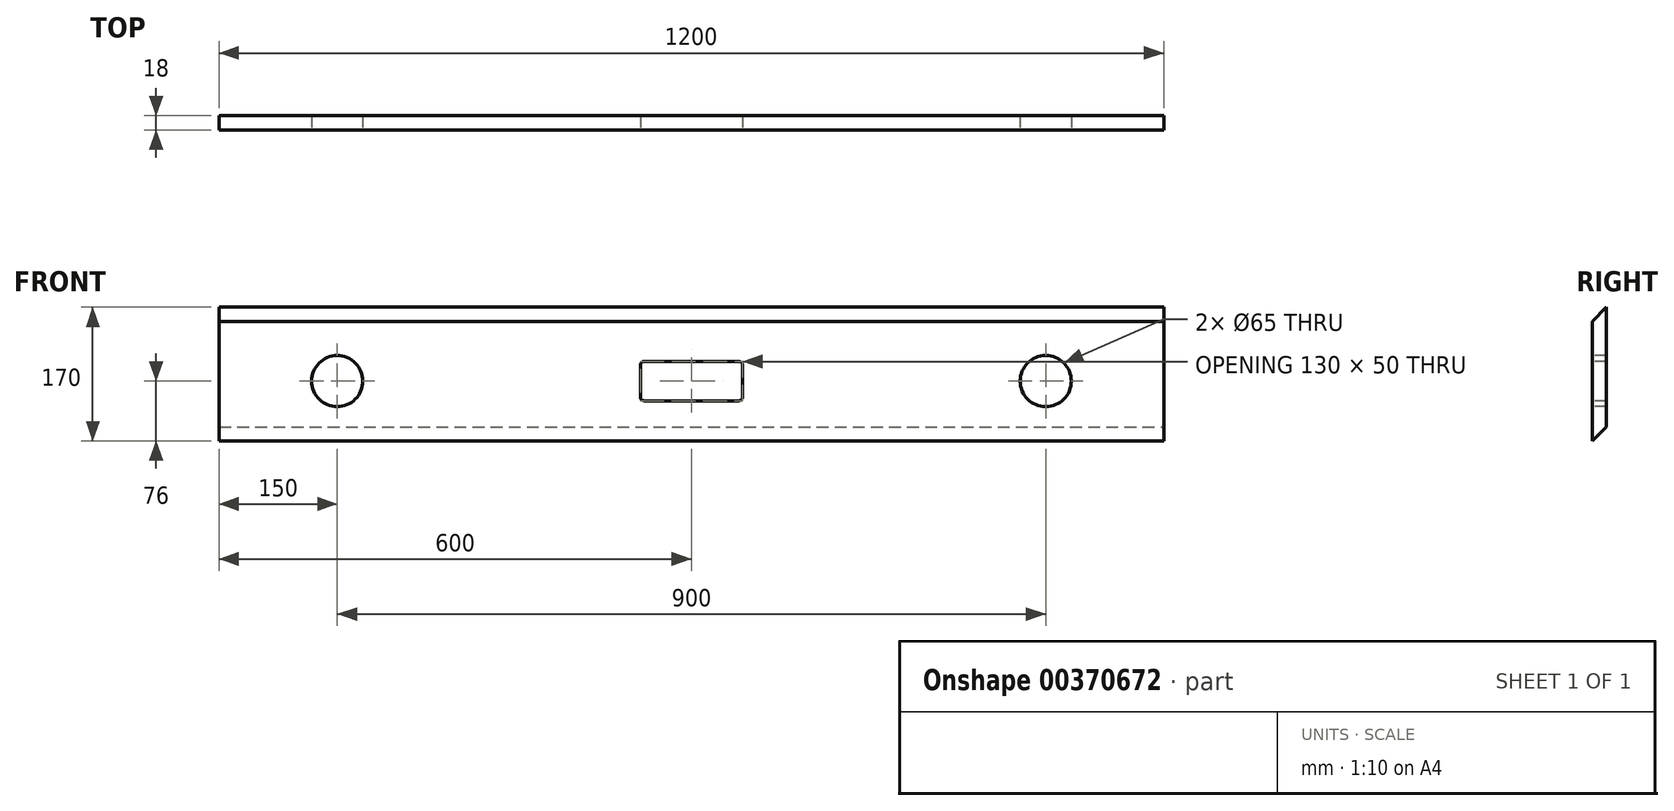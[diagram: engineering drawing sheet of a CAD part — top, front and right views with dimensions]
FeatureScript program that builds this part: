
annotation { "Feature Type Name" : "Feature", "Feature Type Description" : "" }
export const myFeature = defineFeature(function(context is Context, id is Id, definition is map)
    precondition{}
    {
        {
            var Q0;
            Q0=qCreatedBy(makeId("Front.planeOp"),FACE);
            var sketch = newSketch(context, id + "F0", { "sketchPlane" : qUnion([Q0])});
            skLineSegment(sketch, "E0.bottom", {"start": v(0, 0) * mm, "end": v(1200, 0) * mm});
            skLineSegment(sketch, "E0.top", {"start": v(0, 170) * mm, "end": v(1200, 170) * mm});
            skLineSegment(sketch, "E0.left", {"start": v(0, 0) * mm, "end": v(0, 170) * mm});
            skLineSegment(sketch, "E0.right", {"start": v(1200, 0) * mm, "end": v(1200, 170) * mm});
            skSolve(sketch);
        }
        {
            var Q0;
            Q0 = qSketchRegion(id + "F0", true);
            extrude(context, id + "F1", {"entities" : qUnion([Q0]), "depth" : 18 * mm});
        }
        {
            var Q0;
            Q0=makeQuery(id+"F1.opExtrude","SWEPT_FACE",FACE,{"disambiguationData":[OSD([sQuery(id+"F0.wireOp",EDGE,"E0.right")])]});
            var sketch = newSketch(context, id + "F2", { "sketchPlane" : qUnion([Q0])});
            skLineSegment(sketch, "E1", {"start": v(0, 170) * mm, "end": v(-18, 152) * mm});
            skLineSegment(sketch, "E2", {"start": v(-18, 152) * mm, "end": v(-18, 170) * mm});
            skLineSegment(sketch, "E3", {"start": v(-18, 170) * mm, "end": v(0, 170) * mm});
            skLineSegment(sketch, "E4", {"start": v(0, 0) * mm, "end": v(0, 18) * mm});
            skLineSegment(sketch, "E5", {"start": v(0, 18) * mm, "end": v(-18, 0) * mm});
            skLineSegment(sketch, "E6", {"start": v(-18, 0) * mm, "end": v(0, 0) * mm});
            skSolve(sketch);
        }
        {
            var Q0;
            Q0 = qSketchRegion(id + "F2", true);
            extrude(context, id + "F3", {"entities" : qUnion([Q0]), "operationType" : NewBodyOperationType.REMOVE, "endBound" : BoundingType.THROUGH_ALL, "oppositeDirection" : true, "depth" : 25 * mm});
        }
        {
            var Q0;
            Q0=makeQuery(id+"F1.opExtrude","CAP_FACE",FACE,{"disambiguationData":[OSD([sQuery(id+"F0.wireOp",EDGE,"E0.bottom"),sQuery(id+"F0.wireOp",EDGE,"E0.top"),sQuery(id+"F0.wireOp",EDGE,"E0.left"),sQuery(id+"F0.wireOp",EDGE,"E0.right")])],"isStart":false});
            var sketch = newSketch(context, id + "F4", { "sketchPlane" : qUnion([Q0])});
            skLineSegment(sketch, "E7", {"start": v(0, 76) * mm, "end": v(1200, 76) * mm, "construction": true});
            skLineSegment(sketch, "E8", {"start": v(600, 152) * mm, "end": v(600, 0) * mm, "construction": true});
            skCircle(sketch, "E9", {"center": v(150, 76) * mm, "radius": 32.5 * mm});
            skCircle(sketch, "E10", {"center": v(1050, 76) * mm, "radius": 32.5 * mm});
            skLineSegment(sketch, "E11.bottom", {"start": v(660, 51) * mm, "end": v(540, 51) * mm});
            skLineSegment(sketch, "E11.top", {"start": v(660, 101) * mm, "end": v(540, 101) * mm});
            skLineSegment(sketch, "E11.left", {"start": v(665, 56) * mm, "end": v(665, 96) * mm});
            skLineSegment(sketch, "E11.right", {"start": v(535, 56) * mm, "end": v(535, 96) * mm});
            skPoint(sketch, "E11.middle", {"position": v(600, 76) * mm});
            skPoint(sketch, "E12.visualSharp", {"position": v(535, 101) * mm});
            skArc(sketch, "E12.filletArc", {"start": v(540, 101) * mm, "mid": v(536.46, 99.54) * mm, "end": v(535, 96) * mm});
            skPoint(sketch, "E13.visualSharp", {"position": v(535, 51) * mm});
            skArc(sketch, "E13.filletArc", {"start": v(535, 56) * mm, "mid": v(536.46, 52.46) * mm, "end": v(540, 51) * mm});
            skPoint(sketch, "E14.visualSharp", {"position": v(665, 51) * mm});
            skArc(sketch, "E14.filletArc", {"start": v(660, 51) * mm, "mid": v(663.54, 52.46) * mm, "end": v(665, 56) * mm});
            skPoint(sketch, "E15.visualSharp", {"position": v(665, 101) * mm});
            skArc(sketch, "E15.filletArc", {"start": v(665, 96) * mm, "mid": v(663.54, 99.54) * mm, "end": v(660, 101) * mm});
            skSolve(sketch);
        }
        {
            var Q0;
            Q0 = qSketchRegion(id + "F4", true);
            extrude(context, id + "F5", {"entities" : qUnion([Q0]), "operationType" : NewBodyOperationType.REMOVE, "endBound" : BoundingType.THROUGH_ALL, "oppositeDirection" : true, "depth" : 25 * mm});
        }
    });
